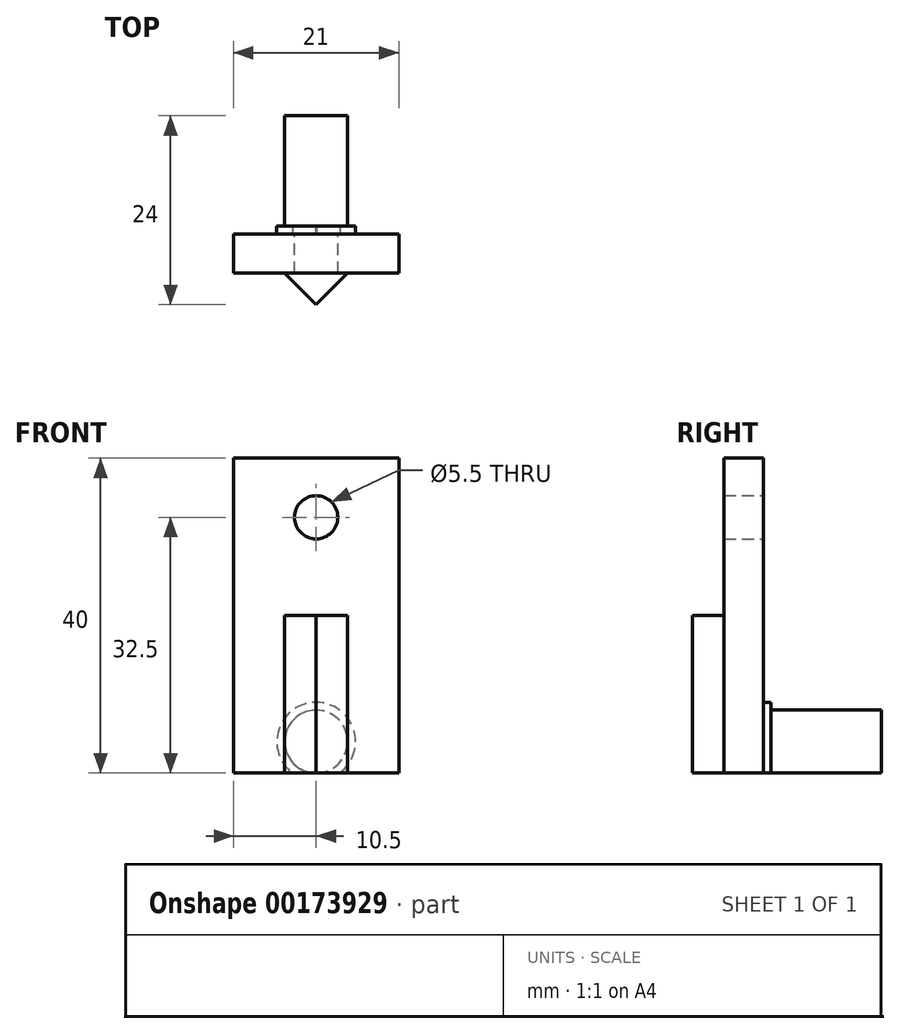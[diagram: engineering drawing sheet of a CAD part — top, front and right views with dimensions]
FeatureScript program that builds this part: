
annotation { "Feature Type Name" : "Feature", "Feature Type Description" : "" }
export const myFeature = defineFeature(function(context is Context, id is Id, definition is map)
    precondition{}
    {
        {
            var Q0;
            Q0=qCreatedBy(makeId("Top.planeOp"),FACE);
            var sketch = newSketch(context, id + "F0", { "sketchPlane" : qUnion([Q0])});
            skLineSegment(sketch, "E0.bottom", {"start": v(-13.5, 0) * mm, "end": v(13.5, 0) * mm});
            skLineSegment(sketch, "E0.top", {"start": v(-13.5, 27) * mm, "end": v(13.5, 27) * mm});
            skLineSegment(sketch, "E0.left", {"start": v(-13.5, 0) * mm, "end": v(-13.5, 27) * mm});
            skLineSegment(sketch, "E0.right", {"start": v(13.5, 0) * mm, "end": v(13.5, 27) * mm});
            skLineSegment(sketch, "E1.top", {"start": v(5, 0) * mm, "end": v(-5, 0) * mm});
            skSolve(sketch);
        }
        {
            var Q0;
            Q0=makeQuery(id+"F0.imprint","IMPRINT",FACE,{"disambiguationData":[TD([[makeQuery(id+"F0.imprint","IMPRINT",EDGE,{"derivedFrom":sQuery(id+"F0.wireOp",EDGE,"E0.bottom")}),1.0]])]});
            var Q1;
            Q1=makeQuery(id+"F0.imprint","IMPRINT",FACE,{"disambiguationData":[TD([[makeQuery(id+"F0.imprint","IMPRINT",EDGE,{"derivedFrom":sQuery(id+"F0.wireOp",EDGE,"E0.top")}),-1.0]])]});
            var Q2;
            Q2=makeQuery(id+"F0.imprint","IMPRINT",FACE,{"disambiguationData":[TD([[makeQuery(id+"F0.imprint","IMPRINT",EDGE,{"derivedFrom":sQuery(id+"F0.wireOp",EDGE,"r3kg0mCG-5yas-oTOn-g2Uv-CVAxs1bjjsDR.top")}),-1.0]])]});
            extrude(context, id + "F1", {"entities" : qUnion([Q0, Q1, Q2]), "depth" : 20 * mm, "offsetDistance" : 25 * mm});
        }
        {
            var Q0;
            Q0=makeQuery(id+"F1.opExtrude","CAP_FACE",FACE,{"disambiguationData":[OSD([sQuery(id+"F0.wireOp",EDGE,"E0.bottom"),sQuery(id+"F0.wireOp",EDGE,"E0.top"),sQuery(id+"F0.wireOp",EDGE,"E0.left"),sQuery(id+"F0.wireOp",EDGE,"E0.right")])],"isStart":false});
            var sketch = newSketch(context, id + "F2", { "sketchPlane" : qUnion([Q0])});
            skLineSegment(sketch, "E2", {"start": v(0, 27) * mm, "end": v(0, 0) * mm});
            skLineSegment(sketch, "E3", {"start": v(-13.5, 11.5) * mm, "end": v(13.5, 11.5) * mm});
            skLineSegment(sketch, "E4.bottom", {"start": v(10.5, 22) * mm, "end": v(-10.5, 22) * mm});
            skLineSegment(sketch, "E4.top", {"start": v(10.5, 1) * mm, "end": v(-10.5, 1) * mm});
            skLineSegment(sketch, "E4.left", {"start": v(10.5, 22) * mm, "end": v(10.5, 1) * mm});
            skLineSegment(sketch, "E4.right", {"start": v(-10.5, 22) * mm, "end": v(-10.5, 1) * mm});
            skPoint(sketch, "E4.middle", {"position": v(0, 11.5) * mm});
            skLineSegment(sketch, "E5", {"start": v(0, 5) * mm, "end": v(-4, 1) * mm});
            skLineSegment(sketch, "E6", {"start": v(0, 5) * mm, "end": v(4, 1) * mm});
            skLineSegment(sketch, "E7.1.0", {"start": v(6.5, 11.5) * mm, "end": v(10.5, 15.5) * mm});
            skLineSegment(sketch, "E7.1.1", {"start": v(6.5, 11.5) * mm, "end": v(10.5, 7.5) * mm});
            skLineSegment(sketch, "E7.2.0", {"start": v(0, 18) * mm, "end": v(-4, 22) * mm});
            skLineSegment(sketch, "E7.2.1", {"start": v(0, 18) * mm, "end": v(4, 22) * mm});
            skLineSegment(sketch, "E7.3.0", {"start": v(-6.5, 11.5) * mm, "end": v(-10.5, 7.5) * mm});
            skLineSegment(sketch, "E7.3.1", {"start": v(-6.5, 11.5) * mm, "end": v(-10.5, 15.5) * mm});
            skLineSegment(sketch, "E8", {"start": v(-10.5, 22) * mm, "end": v(-10.5, 27) * mm});
            skLineSegment(sketch, "E9", {"start": v(10.5, 22) * mm, "end": v(10.5, 27) * mm});
            skSolve(sketch);
        }
        {
            var Q0;
            {var subQ4=sQuery(id+"F2.wireOp",EDGE,"E7.2.0");Q0=makeQuery(id+"F2.imprint","IMPRINT",FACE,{"disambiguationData":[TD([[makeQuery(id+"F2.imprint","IMPRINT",EDGE,{"derivedFrom":subQ4}),1.0]])]});}
            var Q1;
            {var subQ3=sQuery(id+"F2.wireOp",EDGE,"E7.1.0");Q1=makeQuery(id+"F2.imprint","IMPRINT",FACE,{"disambiguationData":[TD([[makeQuery(id+"F2.imprint","IMPRINT",EDGE,{"derivedFrom":subQ3}),1.0]])]});}
            var Q2;
            {var subQ3=sQuery(id+"F2.wireOp",EDGE,"E6");Q2=makeQuery(id+"F2.imprint","IMPRINT",FACE,{"disambiguationData":[TD([[makeQuery(id+"F2.imprint","IMPRINT",EDGE,{"derivedFrom":subQ3}),1.0]])]});}
            var Q3;
            {var subQ4=sQuery(id+"F2.wireOp",EDGE,"E5");Q3=makeQuery(id+"F2.imprint","IMPRINT",FACE,{"disambiguationData":[TD([[makeQuery(id+"F2.imprint","IMPRINT",EDGE,{"derivedFrom":subQ4}),-1.0]])]});}
            var Q4;
            {var subQ0=sQuery(id+"F2.wireOp",EDGE,"E5");Q4=makeQuery(id+"F2.imprint","IMPRINT",FACE,{"disambiguationData":[TD([[makeQuery(id+"F2.imprint","IMPRINT",EDGE,{"derivedFrom":subQ0}),1.0]])]});}
            var Q5;
            {var subQ0=sQuery(id+"F2.wireOp",EDGE,"E6");Q5=makeQuery(id+"F2.imprint","IMPRINT",FACE,{"disambiguationData":[TD([[makeQuery(id+"F2.imprint","IMPRINT",EDGE,{"derivedFrom":subQ0}),-1.0]])]});}
            var Q6;
            {var subQ0=sQuery(id+"F2.wireOp",EDGE,"E7.3.1");Q6=makeQuery(id+"F2.imprint","IMPRINT",FACE,{"disambiguationData":[TD([[makeQuery(id+"F2.imprint","IMPRINT",EDGE,{"derivedFrom":subQ0}),1.0]])]});}
            var Q7;
            {var subQ0=sQuery(id+"F2.wireOp",EDGE,"E7.3.0");Q7=makeQuery(id+"F2.imprint","IMPRINT",FACE,{"disambiguationData":[TD([[makeQuery(id+"F2.imprint","IMPRINT",EDGE,{"derivedFrom":subQ0}),-1.0]])]});}
            var Q8;
            {var subQ4=sQuery(id+"F2.wireOp",EDGE,"E8");Q8=makeQuery(id+"F2.imprint","IMPRINT",FACE,{"disambiguationData":[TD([[makeQuery(id+"F2.imprint","IMPRINT",EDGE,{"derivedFrom":subQ4}),1.0]])]});}
            var Q9;
            {var subQ6=sQuery(id+"F2.wireOp",EDGE,"E3");var subQ7=makeQuery(id+"F1.opExtrude","CAP_EDGE",EDGE,{"disambiguationData":[OSD([sQuery(id+"F0.wireOp",EDGE,"E0.left")])],"isStart":false});var subQ8=makeQuery(id+"F2.imprint","INTERSECT",VERTEX,{"derivedFrom":[subQ7,subQ6]});Q9=makeQuery(id+"F2.imprint","IMPRINT",FACE,{"disambiguationData":[TD([[makeQuery(id+"F2.imprint","IMPRINT",EDGE,{"disambiguationData":[TD([[subQ8,-1.0]])],"derivedFrom":subQ6}),-1.0]])]});}
            var Q10;
            {var subQ4=makeQuery(id+"F1.opExtrude","CAP_EDGE",EDGE,{"disambiguationData":[OSD([sQuery(id+"F0.wireOp",EDGE,"E0.right")])],"isStart":false});var subQ10=sQuery(id+"F2.wireOp",EDGE,"E3");var subQ11=makeQuery(id+"F2.imprint","INTERSECT",VERTEX,{"derivedFrom":[subQ4,subQ10]});Q10=makeQuery(id+"F2.imprint","IMPRINT",FACE,{"disambiguationData":[TD([[makeQuery(id+"F2.imprint","IMPRINT",EDGE,{"disambiguationData":[TD([[subQ11,1.0]])],"derivedFrom":subQ10}),-1.0]])]});}
            var Q11;
            {var subQ0=sQuery(id+"F2.wireOp",EDGE,"E9");Q11=makeQuery(id+"F2.imprint","IMPRINT",FACE,{"disambiguationData":[TD([[makeQuery(id+"F2.imprint","IMPRINT",EDGE,{"derivedFrom":subQ0}),-1.0]])]});}
            var Q12;
            {var subQ0=sQuery(id+"F2.wireOp",EDGE,"E7.1.0");Q12=makeQuery(id+"F2.imprint","IMPRINT",FACE,{"disambiguationData":[TD([[makeQuery(id+"F2.imprint","IMPRINT",EDGE,{"derivedFrom":subQ0}),-1.0]])]});}
            var Q13;
            {var subQ0=sQuery(id+"F2.wireOp",EDGE,"E7.1.1");Q13=makeQuery(id+"F2.imprint","IMPRINT",FACE,{"disambiguationData":[TD([[makeQuery(id+"F2.imprint","IMPRINT",EDGE,{"derivedFrom":subQ0}),1.0]])]});}
            extrude(context, id + "F3", {"entities" : qUnion([Q0, Q1, Q2, Q3, Q4, Q5, Q6, Q7, Q8, Q9, Q10, Q11, Q12, Q13]), "operationType" : NewBodyOperationType.REMOVE, "endBound" : BoundingType.THROUGH_ALL, "oppositeDirection" : true, "depth" : 25 * mm, "offsetDistance" : 25 * mm});
        }
        {
            var Q0;
            Q0=makeQuery(id+"F1.opExtrude","SWEPT_FACE",FACE,{"disambiguationData":[OSD([sQuery(id+"F0.wireOp",EDGE,"E0.top")])]});
            var sketch = newSketch(context, id + "F4", { "sketchPlane" : qUnion([Q0])});
            skCircle(sketch, "E10", {"center": v(0, 4) * mm, "radius": 4 * mm});
            skCircle(sketch, "E11", {"center": v(0, 4) * mm, "radius": 5 * mm});
            skLineSegment(sketch, "E12", {"start": v(0.05, 0) * mm, "end": v(-3, 0) * mm});
            skLineSegment(sketch, "E13", {"start": v(-0.05, 0) * mm, "end": v(-0.05, 0) * mm});
            skLineSegment(sketch, "E14", {"start": v(0.05, 0) * mm, "end": v(0.05, 0) * mm});
            skSolve(sketch);
        }
        {
            var Q0;
            {var subQ0=sQuery(id+"F4.wireOp",EDGE,"E13");Q0=makeQuery(id+"F4.imprint","IMPRINT",FACE,{"disambiguationData":[TD([[makeQuery(id+"F4.imprint","IMPRINT",EDGE,{"derivedFrom":subQ0}),1.0]])]});}
            extrude(context, id + "F5", {"entities" : qUnion([Q0]), "operationType" : NewBodyOperationType.ADD, "depth" : 1 * mm, "offsetDistance" : 25 * mm});
        }
        {
            var Q0;
            Q0=makeQuery(id+"F4.imprint","IMPRINT",FACE,{"disambiguationData":[TD([[makeQuery(id+"F4.imprint","IMPRINT",EDGE,{"derivedFrom":sQuery(id+"F4.wireOp",EDGE,"E10")}),1.0]])]});
            extrude(context, id + "F6", {"entities" : qUnion([Q0]), "operationType" : NewBodyOperationType.ADD, "depth" : 15 * mm, "offsetDistance" : 25 * mm});
        }
        {
            var Q0;
            Q0=makeQuery(id+"F1.opExtrude","CAP_FACE",FACE,{"disambiguationData":[OSD([sQuery(id+"F0.wireOp",EDGE,"E0.bottom"),sQuery(id+"F0.wireOp",EDGE,"E0.top"),sQuery(id+"F0.wireOp",EDGE,"E0.left"),sQuery(id+"F0.wireOp",EDGE,"E0.right"),sQuery(id+"F0.wireOp",EDGE,"E1.top")])],"isStart":false});
            var sketch = newSketch(context, id + "F7", { "sketchPlane" : qUnion([Q0])});
            skLineSegment(sketch, "E15.bottom", {"start": v(-10.5, 22) * mm, "end": v(10.5, 22) * mm});
            skLineSegment(sketch, "E15.top", {"start": v(-10.5, 27) * mm, "end": v(10.5, 27) * mm});
            skLineSegment(sketch, "E15.left", {"start": v(-10.5, 22) * mm, "end": v(-10.5, 27) * mm});
            skLineSegment(sketch, "E15.right", {"start": v(10.5, 22) * mm, "end": v(10.5, 27) * mm});
            skSolve(sketch);
        }
        {
            var Q0;
            Q0 = qSketchRegion(id + "F7", true);
            extrude(context, id + "F8", {"entities" : qUnion([Q0]), "operationType" : NewBodyOperationType.ADD, "depth" : 20 * mm, "offsetDistance" : 25 * mm});
        }
        {
            var Q0;
            {var subQ3=sQuery(id+"F0.wireOp",EDGE,"E0.top");Q0=makeQuery(id+"F8.boolean.opBoolean","MERGE",FACE,{"derivedFrom":[makeQuery(id+"F5.boolean.opBoolean","SPLIT",FACE,{"disambiguationData":[TD([makeQuery(id+"F3.boolean.opBoolean","COPY",FACE,{"derivedFrom":makeQuery(id+"F3.opExtrude","SWEPT_FACE",FACE,{"disambiguationData":[OSD([sQuery(id+"F2.wireOp",EDGE,"E8")])]})})])],"derivedFrom":makeQuery(id+"F1.opExtrude","SWEPT_FACE",FACE,{"disambiguationData":[OSD([subQ3])]})}),makeQuery(id+"F8.opExtrude","SWEPT_FACE",FACE,{"disambiguationData":[OSD([sQuery(id+"F7.wireOp",EDGE,"E15.top")])]})]});}
            var sketch = newSketch(context, id + "F9", { "sketchPlane" : qUnion([Q0])});
            skLineSegment(sketch, "E16.bottom", {"start": v(-10.5, 40) * mm, "end": v(10.5, 40) * mm});
            skLineSegment(sketch, "E16.top", {"start": v(-10.5, 25) * mm, "end": v(10.5, 25) * mm});
            skLineSegment(sketch, "E16.left", {"start": v(-10.5, 40) * mm, "end": v(-10.5, 25) * mm});
            skLineSegment(sketch, "E16.right", {"start": v(10.5, 40) * mm, "end": v(10.5, 25) * mm});
            skPoint(sketch, "E16.middle", {"position": v(0, 32.5) * mm});
            skSolve(sketch);
        }
        {
            var Q0;
            Q0=sQuery(id+"F9.wireOp",VERTEX,"E16.middle");
            var Q1;
            Q1=makeQuery(id+"F1.opExtrude","SWEPT_BODY",BODY,{"disambiguationData":[OSD([sQuery(id+"F0.wireOp",EDGE,"xHkcvzyH-9kmu-wbCr-jR9n-D6HEL6nOpGrQ"),sQuery(id+"F0.wireOp",EDGE,"HCY4NaYE-prSY-boik-VQEE-KTlIMcDiN2et"),sQuery(id+"F0.wireOp",EDGE,"WuNqzkiV-5fIL-Ygxi-hsma-e7T6jagV0e0Y"),sQuery(id+"F0.wireOp",EDGE,"2OK0SqrW-3Etj-5ayL-7rRH-hWcyb4yQmMM4"),sQuery(id+"F0.wireOp",EDGE,"lwhvDbMa-AmNj-0qt0-y0KF-N0vn7AxuHUuw"),sQuery(id+"F0.wireOp",EDGE,"Bpkg6DPL-H1ym-XptN-jvIf-c3K8TXIWIoFH"),sQuery(id+"F0.wireOp",EDGE,"hlCVzPfB-2dpC-Jpgm-U181-AJxs24huhhLZ"),sQuery(id+"F0.wireOp",EDGE,"8QqTi3ct-ThRm-gueO-aHDC-F4Muzk4KxUct.top"),sQuery(id+"F0.wireOp",EDGE,"8QqTi3ct-ThRm-gueO-aHDC-F4Muzk4KxUct.left"),sQuery(id+"F0.wireOp",EDGE,"8QqTi3ct-ThRm-gueO-aHDC-F4Muzk4KxUct.right"),sQuery(id+"F0.wireOp",EDGE,"d1653463-5d28-4219-b4a5-8c73052c44480.MirrorCS"),sQuery(id+"F0.wireOp",EDGE,"8604e583-d332-466a-8dde-0e841fae2b530.MirrorCS"),sQuery(id+"F0.wireOp",EDGE,"2614f8c5-c022-48f9-b6df-9e0814651a8c0.MirrorCS"),sQuery(id+"F0.wireOp",EDGE,"EvqpzCpu-QXtl-eKPM-fO3z-jtB7Z1EKyX8v"),sQuery(id+"F0.wireOp",EDGE,"TuMM16le-KGyB-roy2-t4tL-9nZMhsLml1HU")])]});
            var Q2;
            Q2=makeQuery(id+"F1.opExtrude","SWEPT_BODY",BODY,{"disambiguationData":[OSD([sQuery(id+"F0.wireOp",EDGE,"E0.top"),sQuery(id+"F0.wireOp",EDGE,"E0.left"),sQuery(id+"F0.wireOp",EDGE,"E0.right"),sQuery(id+"F0.wireOp",EDGE,"r3kg0mCG-5yas-oTOn-g2Uv-CVAxs1bjjsDR.bottom"),sQuery(id+"F0.wireOp",EDGE,"r3kg0mCG-5yas-oTOn-g2Uv-CVAxs1bjjsDR.top"),sQuery(id+"F0.wireOp",EDGE,"r3kg0mCG-5yas-oTOn-g2Uv-CVAxs1bjjsDR.left"),sQuery(id+"F0.wireOp",EDGE,"r3kg0mCG-5yas-oTOn-g2Uv-CVAxs1bjjsDR.right"),sQuery(id+"F0.wireOp",EDGE,"E1.top"),sQuery(id+"F0.wireOp",EDGE,"E1.left"),sQuery(id+"F0.wireOp",EDGE,"E1.right")])]});
            hole(context, id + "F10", {"style" : HoleStyle.SIMPLE, "endStyle" : HoleEndStyle.BLIND, "standardTappedOrClearance" : lookupTablePath({ "standard" : "ISO", "fit" : "Normal", "size" : "M5", "type" : "Clearance" }), "standardBlindInLast" : lookupTablePath({ "fit" : "Standard", "standard" : "ISO", "size" : "M5", "type" : "Clearance" }), "holeDiameter" : 5.5 * mm, "majorDiameter" : 5 * mm, "holeDepth" : 12 * mm, "locations" : qUnion([Q0]), "scope" : qUnion([Q1, Q2]), "tappedDepth" : 12 * mm, "tapClearance" : 3});
        }
    });
